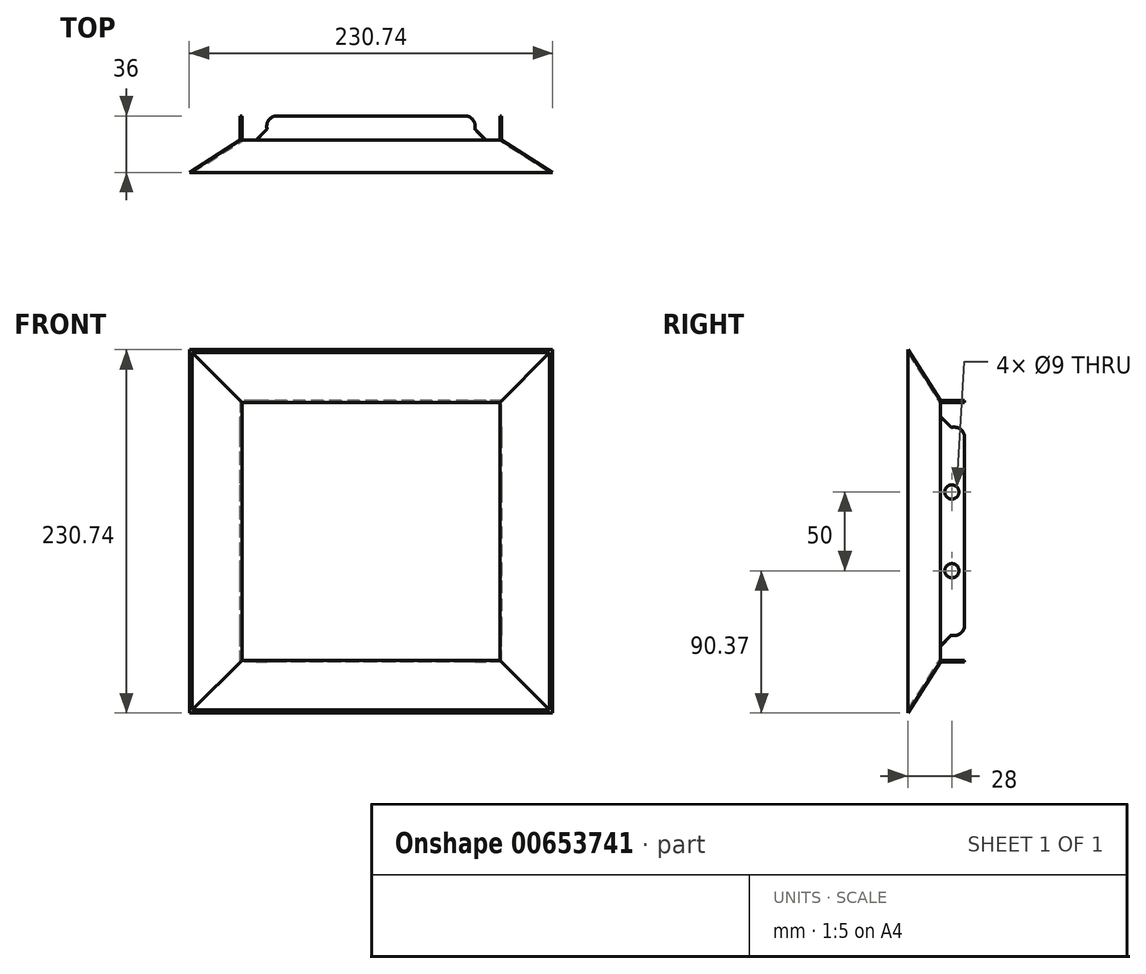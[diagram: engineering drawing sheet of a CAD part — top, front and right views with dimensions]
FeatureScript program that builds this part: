
annotation { "Feature Type Name" : "Feature", "Feature Type Description" : "" }
export const myFeature = defineFeature(function(context is Context, id is Id, definition is map)
    precondition{}
    {
        {
            var Q0;
            Q0=qCreatedBy(makeId("Front.planeOp"),FACE);
            var sketch = newSketch(context, id + "F0", { "sketchPlane" : qUnion([Q0])});
            skLineSegment(sketch, "E0.bottom", {"start": v(118.5, 118.5) * mm, "end": v(-118.5, 118.5) * mm});
            skLineSegment(sketch, "E0.top", {"start": v(118.5, -118.5) * mm, "end": v(-118.5, -118.5) * mm});
            skLineSegment(sketch, "E0.left", {"start": v(118.5, 118.5) * mm, "end": v(118.5, -118.5) * mm});
            skLineSegment(sketch, "E0.right", {"start": v(-118.5, 118.5) * mm, "end": v(-118.5, -118.5) * mm});
            skPoint(sketch, "E0.middle", {"position": v(0, 0) * mm});
            skLineSegment(sketch, "E1.bottom", {"start": v(-113.5, 113.5) * mm, "end": v(113.5, 113.5) * mm});
            skLineSegment(sketch, "E1.top", {"start": v(-113.5, -113.5) * mm, "end": v(113.5, -113.5) * mm});
            skLineSegment(sketch, "E1.left", {"start": v(-113.5, 113.5) * mm, "end": v(-113.5, -113.5) * mm});
            skLineSegment(sketch, "E1.right", {"start": v(113.5, 113.5) * mm, "end": v(113.5, -113.5) * mm});
            skSolve(sketch);
        }
        {
            var Q0;
            Q0=qCreatedBy(makeId("Front.planeOp"),FACE);
            cPlane(context, id + "F1", {"entities" : qUnion([Q0]), "cplaneType" : CPlaneType.OFFSET, "offset" : 20 * mm, "oppositeDirection" : true, "width" : 150 * mm, "height" : 150 * mm});
        }
        {
            var Q0;
            Q0=qCreatedBy(id+"F1.planeOp",FACE);
            var sketch = newSketch(context, id + "F2", { "sketchPlane" : qUnion([Q0])});
            skLineSegment(sketch, "E2.bottom", {"start": v(82, 82) * mm, "end": v(-82, 82) * mm});
            skLineSegment(sketch, "E2.top", {"start": v(82, -82) * mm, "end": v(-82, -82) * mm});
            skLineSegment(sketch, "E2.left", {"start": v(82, 82) * mm, "end": v(82, -82) * mm});
            skLineSegment(sketch, "E2.right", {"start": v(-82, 82) * mm, "end": v(-82, -82) * mm});
            skPoint(sketch, "E2.middle", {"position": v(0, 0) * mm});
            skSolve(sketch);
        }
        {
            var Q0;
            Q0=makeQuery(id+"F0.imprint","IMPRINT",FACE,{"disambiguationData":[TD([[makeQuery(id+"F0.imprint","IMPRINT",EDGE,{"derivedFrom":sQuery(id+"F0.wireOp",EDGE,"E1.bottom")}),-1.0]])]});
            var Q1;
            Q1=makeQuery(id+"F2.imprint","IMPRINT",FACE,{"disambiguationData":[TD([[makeQuery(id+"F2.imprint","IMPRINT",EDGE,{"derivedFrom":sQuery(id+"F2.wireOp",EDGE,"E2.bottom")}),1.0]])]});
            loft(context, id + "F3", {"sheetProfilesArray" : [{ "sheetProfileEntities" : qUnion([Q0]) }, { "sheetProfileEntities" : qUnion([Q1]) }]});
        }
        {
            var Q0;
            Q0=qCreatedBy(id+"F1.planeOp",FACE);
            cPlane(context, id + "F4", {"entities" : qUnion([Q0]), "cplaneType" : CPlaneType.OFFSET, "offset" : 16 * mm, "oppositeDirection" : true, "width" : 150 * mm, "height" : 150 * mm});
        }
        {
            var Q0;
            Q0=qCreatedBy(id+"F4.planeOp",FACE);
            var sketch = newSketch(context, id + "F5", { "sketchPlane" : qUnion([Q0])});
            skLineSegment(sketch, "E3.0.0", {"start": v(82, -82) * mm, "end": v(-82, -82) * mm});
            skLineSegment(sketch, "E3.0.1", {"start": v(-82, -82) * mm, "end": v(-82, 82) * mm});
            skLineSegment(sketch, "E3.0.2", {"start": v(-82, 82) * mm, "end": v(82, 82) * mm});
            skLineSegment(sketch, "E3.0.3", {"start": v(82, 82) * mm, "end": v(82, -82) * mm});
            skSolve(sketch);
        }
        {
            var Q1;
            Q1=makeQuery(id+"F5.imprint","IMPRINT",FACE,{"disambiguationData":[TD([[makeQuery(id+"F5.imprint","IMPRINT",EDGE,{"derivedFrom":sQuery(id+"F5.wireOp",EDGE,"E3.0.0")}),-1.0]])]});
            var Q2;
            Q2=makeQuery(id+"F3.opLoft","CAP_FACE",FACE,{"disambiguationData":[OSD([makeQuery(id+"F2.imprint","IMPRINT",FACE,{"disambiguationData":[TD([[makeQuery(id+"F2.imprint","IMPRINT",EDGE,{"derivedFrom":sQuery(id+"F2.wireOp",EDGE,"E2.bottom")}),1.0]])]})])],"isStart":true});
            loft(context, id + "F6", {"operationType" : NewBodyOperationType.ADD, "sheetProfilesArray" : [{ "sheetProfileEntities" : qUnion([Q1]) }, { "sheetProfileEntities" : qUnion([Q2]) }]});
        }
        {
            var Q0;
            Q0=makeQuery(id+"F3.opLoft","CAP_FACE",FACE,{"disambiguationData":[OSD([makeQuery(id+"F0.imprint","IMPRINT",FACE,{"disambiguationData":[TD([[makeQuery(id+"F0.imprint","IMPRINT",EDGE,{"derivedFrom":sQuery(id+"F0.wireOp",EDGE,"E1.bottom")}),-1.0]])]})])],"isStart":true});
            var Q1;
            Q1=makeQuery(id+"F6.opLoft","CAP_FACE",FACE,{"disambiguationData":[OSD([makeQuery(id+"F5.imprint","IMPRINT",FACE,{"disambiguationData":[TD([[makeQuery(id+"F5.imprint","IMPRINT",EDGE,{"derivedFrom":sQuery(id+"F5.wireOp",EDGE,"E3.0.0")}),-1.0]])]})])],"isStart":true});
            shell(context, id + "F7", {"entities" : qUnion([Q0, Q1]), "thickness" : 1 * mm, "oppositeDirection" : true});
        }
        {
            var Q0;
            Q0=makeQuery(id+"F6.opLoft","SWEPT_FACE",FACE,{"disambiguationData":[OSD([sQuery(id+"F2.wireOp",EDGE,"E2.bottom"),sQuery(id+"F2.wireOp",EDGE,"E2.top"),sQuery(id+"F2.wireOp",EDGE,"E2.right"),sQuery(id+"F5.wireOp",EDGE,"E3.0.0"),sQuery(id+"F5.wireOp",EDGE,"E3.0.1"),sQuery(id+"F5.wireOp",EDGE,"E3.0.2")])]});
            var sketch = newSketch(context, id + "F8", { "sketchPlane" : qUnion([Q0])});
            skLineSegment(sketch, "E4", {"start": v(-20.55, 83) * mm, "end": v(-20.55, 73) * mm});
            skLineSegment(sketch, "E5", {"start": v(-20.55, 73) * mm, "end": v(-27.62, 65.93) * mm});
            skArc(sketch, "E6", {"start": v(-27.62, 65.93) * mm, "mid": v(-33.79, 64.53) * mm, "end": v(-36, 58.6) * mm});
            skLineSegment(sketch, "E7", {"start": v(-20.55, 83) * mm, "end": v(-36, 83) * mm});
            skLineSegment(sketch, "E8", {"start": v(-36, 83) * mm, "end": v(-36, 58.6) * mm});
            skLineSegment(sketch, "E9.MirrorCS", {"start": v(-20.55, -83) * mm, "end": v(-36, -83) * mm});
            skArc(sketch, "E10.MirrorCS", {"start": v(-27.62, -65.93) * mm, "mid": v(-33.79, -64.53) * mm, "end": v(-36, -58.6) * mm});
            skLineSegment(sketch, "E11.MirrorCS", {"start": v(-20.55, -83) * mm, "end": v(-20.55, -73) * mm});
            skLineSegment(sketch, "E12.MirrorCS", {"start": v(-20.55, -73) * mm, "end": v(-27.62, -65.93) * mm});
            skLineSegment(sketch, "E13.MirrorCS", {"start": v(-36, -83) * mm, "end": v(-36, -58.6) * mm});
            skSolve(sketch);
        }
        {
            var Q0;
            Q0=makeQuery(id+"F8.imprint","IMPRINT",FACE,{"disambiguationData":[TD([[makeQuery(id+"F8.imprint","IMPRINT",EDGE,{"derivedFrom":sQuery(id+"F8.wireOp",EDGE,"E4")}),1.0]])]});
            var Q1;
            Q1=sQuery(id+"F8.wireOp",EDGE,"E7");
            revolve(context, id + "F9", {"operationType" : NewBodyOperationType.REMOVE, "entities" : qUnion([Q0]), "axis" : qUnion([Q1]), "revolveType" : RevolveType.FULL, "oppositeDirection" : true});
        }
        {
            var Q0;
            {var subQ4=sQuery(id+"F8.wireOp",EDGE,"E9.MirrorCS");Q0=makeQuery(id+"F8.imprint","IMPRINT",FACE,{"disambiguationData":[TD([[makeQuery(id+"F8.imprint","IMPRINT",EDGE,{"derivedFrom":subQ4}),1.0]])]});}
            var Q1;
            Q1=sQuery(id+"F8.wireOp",EDGE,"E9.MirrorCS");
            revolve(context, id + "F10", {"operationType" : NewBodyOperationType.REMOVE, "entities" : qUnion([Q0]), "axis" : qUnion([Q1]), "revolveType" : RevolveType.FULL, "oppositeDirection" : true});
        }
        {
            var Q0;
            Q0=makeQuery(id+"F6.opLoft","SWEPT_FACE",FACE,{"disambiguationData":[OSD([sQuery(id+"F2.wireOp",EDGE,"E2.bottom"),sQuery(id+"F2.wireOp",EDGE,"E2.top"),sQuery(id+"F2.wireOp",EDGE,"E2.left"),sQuery(id+"F5.wireOp",EDGE,"E3.0.0"),sQuery(id+"F5.wireOp",EDGE,"E3.0.2"),sQuery(id+"F5.wireOp",EDGE,"E3.0.3")])]});
            var sketch = newSketch(context, id + "F11", { "sketchPlane" : qUnion([Q0])});
            skLineSegment(sketch, "E14.0", {"start": v(20.55, -73) * mm, "end": v(27.62, -65.93) * mm});
            skArc(sketch, "E15.0", {"start": v(27.62, -65.93) * mm, "mid": v(33.79, -64.53) * mm, "end": v(36, -58.6) * mm});
            skLineSegment(sketch, "E16.0", {"start": v(20.55, -83) * mm, "end": v(20.55, -73) * mm});
            skLineSegment(sketch, "E17.0", {"start": v(20.55, -83) * mm, "end": v(36, -83) * mm});
            skLineSegment(sketch, "E18.0", {"start": v(36, -83) * mm, "end": v(36, -58.6) * mm});
            skLineSegment(sketch, "E19.MirrorCS", {"start": v(20.55, 83) * mm, "end": v(20.55, 73) * mm});
            skLineSegment(sketch, "E20.MirrorCS", {"start": v(20.55, 83) * mm, "end": v(36, 83) * mm});
            skLineSegment(sketch, "E21.MirrorCS", {"start": v(20.55, 73) * mm, "end": v(27.62, 65.93) * mm});
            skLineSegment(sketch, "E22.MirrorCS", {"start": v(36, 83) * mm, "end": v(36, 58.6) * mm});
            skArc(sketch, "E23.MirrorCS", {"start": v(27.62, 65.93) * mm, "mid": v(33.79, 64.53) * mm, "end": v(36, 58.6) * mm});
            skSolve(sketch);
        }
        {
            var Q0;
            {var subQ2=sQuery(id+"F11.wireOp",EDGE,"E14.0");Q0=makeQuery(id+"F11.imprint","IMPRINT",FACE,{"disambiguationData":[TD([[makeQuery(id+"F11.imprint","IMPRINT",EDGE,{"derivedFrom":subQ2}),-1.0]])]});}
            var Q1;
            Q1=sQuery(id+"F11.wireOp",EDGE,"E17.0");
            revolve(context, id + "F12", {"operationType" : NewBodyOperationType.REMOVE, "entities" : qUnion([Q0]), "axis" : qUnion([Q1]), "revolveType" : RevolveType.FULL, "oppositeDirection" : true});
        }
        {
            var Q0;
            Q0=makeQuery(id+"F11.imprint","IMPRINT",FACE,{"disambiguationData":[TD([[makeQuery(id+"F11.imprint","IMPRINT",EDGE,{"derivedFrom":sQuery(id+"F11.wireOp",EDGE,"E19.MirrorCS")}),1.0]])]});
            var Q1;
            Q1=sQuery(id+"F11.wireOp",EDGE,"E20.MirrorCS");
            revolve(context, id + "F13", {"operationType" : NewBodyOperationType.REMOVE, "entities" : qUnion([Q0]), "axis" : qUnion([Q1]), "revolveType" : RevolveType.FULL, "oppositeDirection" : true});
        }
        {
            var Q0;
            {var subQ2=sQuery(id+"F11.wireOp",EDGE,"E14.0");Q0=makeQuery(id+"F11.imprint","IMPRINT",FACE,{"disambiguationData":[TD([[makeQuery(id+"F11.imprint","IMPRINT",EDGE,{"derivedFrom":subQ2}),1.0]])]});}
            var sketch = newSketch(context, id + "F14", { "sketchPlane" : qUnion([Q0])});
            skCircle(sketch, "E24", {"center": v(28, 25) * mm, "radius": 4.5 * mm});
            skCircle(sketch, "E25", {"center": v(28, -25) * mm, "radius": 4.5 * mm});
            skSolve(sketch);
        }
        {
            var Q0;
            Q0=qSketchRegion(id+"F14",true);
            extrude(context, id + "F15", {"entities" : qUnion([Q0]), "operationType" : NewBodyOperationType.REMOVE, "endBound" : BoundingType.THROUGH_ALL, "oppositeDirection" : true, "depth" : 25 * mm});
        }
    });
